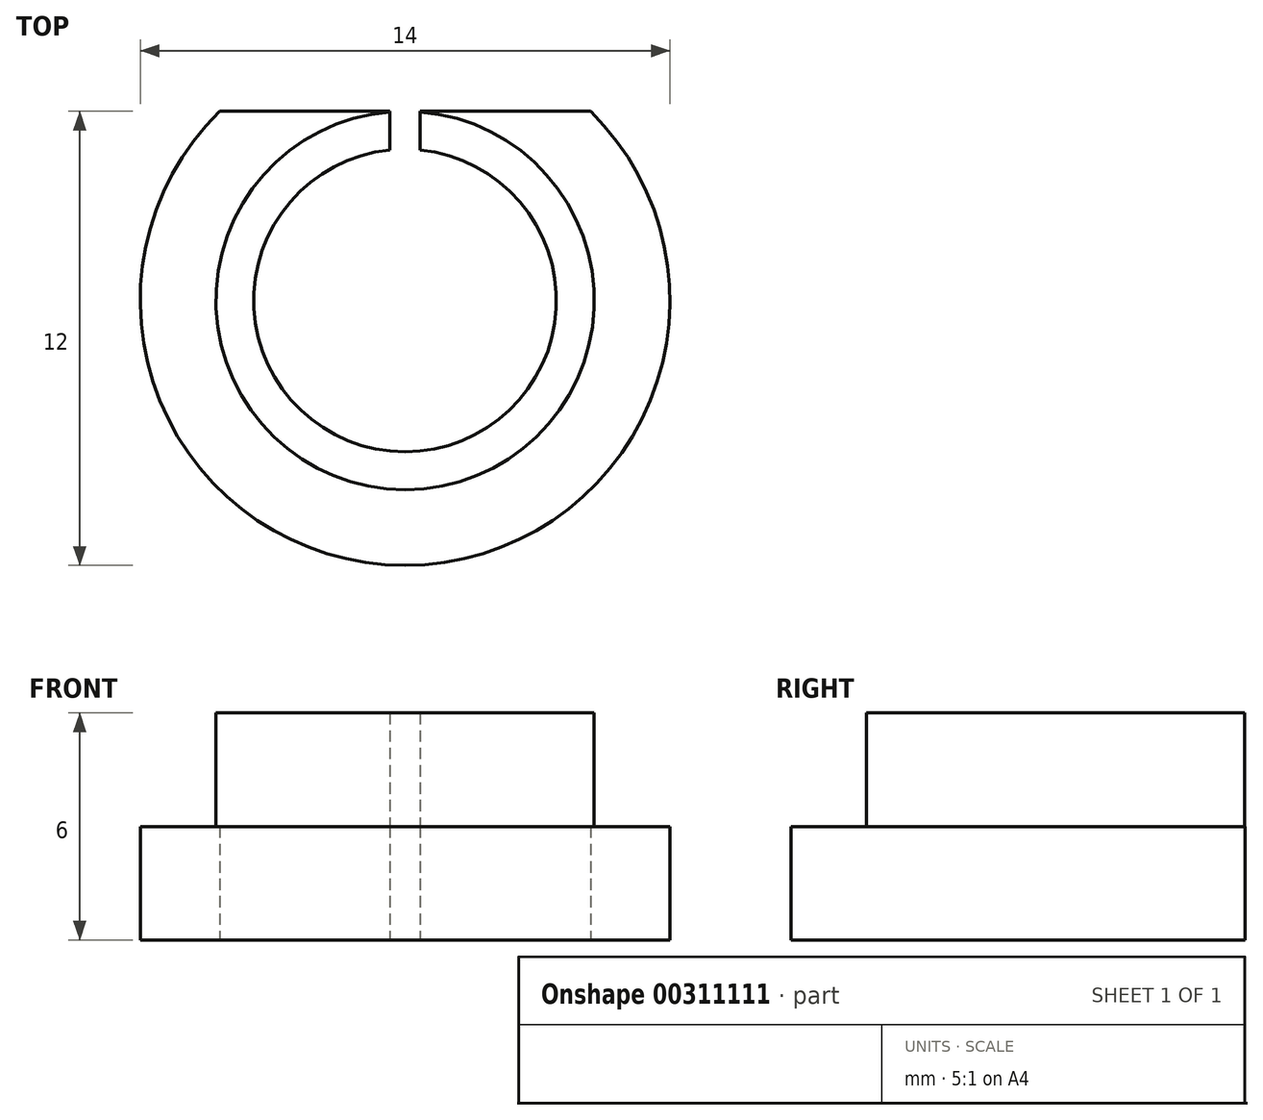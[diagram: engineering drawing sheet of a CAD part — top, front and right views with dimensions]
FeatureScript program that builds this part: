
annotation { "Feature Type Name" : "Feature", "Feature Type Description" : "" }
export const myFeature = defineFeature(function(context is Context, id is Id, definition is map)
    precondition{}
    {
        {
            var Q0;
            Q0=qCreatedBy(makeId("Top.planeOp"),FACE);
            var sketch = newSketch(context, id + "F0", { "sketchPlane" : qUnion([Q0])});
            skCircle(sketch, "E0", {"center": v(0, 0) * mm, "radius": 4 * mm});
            skCircle(sketch, "E1", {"center": v(0, 0) * mm, "radius": 7 * mm});
            skSolve(sketch);
        }
        {
            var Q0;
            Q0 = qSketchRegion(id + "F0", true);
            extrude(context, id + "F1", {"entities" : qUnion([Q0]), "depth" : 3 * mm});
        }
        {
            var Q0;
            Q0=makeQuery(id+"F1.opExtrude","CAP_FACE",FACE,{"disambiguationData":[OSD([sQuery(id+"F0.wireOp",EDGE,"E0"),sQuery(id+"F0.wireOp",EDGE,"E1")])],"isStart":false});
            var sketch = newSketch(context, id + "F2", { "sketchPlane" : qUnion([Q0])});
            skCircle(sketch, "E2", {"center": v(0, 0) * mm, "radius": 4 * mm});
            skCircle(sketch, "E3", {"center": v(0, 0) * mm, "radius": 5 * mm});
            skSolve(sketch);
        }
        {
            var Q0;
            Q0 = qSketchRegion(id + "F2", true);
            extrude(context, id + "F3", {"entities" : qUnion([Q0]), "operationType" : NewBodyOperationType.ADD, "depth" : 3 * mm});
        }
        {
            var Q0;
            Q0=qCreatedBy(makeId("Top.planeOp"),FACE);
            var sketch = newSketch(context, id + "F4", { "sketchPlane" : qUnion([Q0])});
            skArc(sketch, "E4.0", {"start": v(4.9, 5) * mm, "mid": v(0, 7) * mm, "end": v(-4.9, 5) * mm});
            skLineSegment(sketch, "E5", {"start": v(0, 5) * mm, "end": v(4.9, 5) * mm});
            skLineSegment(sketch, "E6", {"start": v(0, 5) * mm, "end": v(-4.9, 5) * mm});
            skLineSegment(sketch, "E7", {"start": v(-0.4, 5) * mm, "end": v(-0.4, 3.38) * mm});
            skLineSegment(sketch, "E8", {"start": v(-0.4, 3.38) * mm, "end": v(0.4, 3.38) * mm});
            skLineSegment(sketch, "E9", {"start": v(0.4, 3.38) * mm, "end": v(0.4, 5) * mm});
            skSolve(sketch);
        }
        {
            var Q0;
            Q0 = qSketchRegion(id + "F4", true);
            var Q1;
            Q1=makeQuery(id+"F3.opExtrude","CAP_FACE",FACE,{"disambiguationData":[OSD([sQuery(id+"F2.wireOp",EDGE,"E2"),sQuery(id+"F2.wireOp",EDGE,"E3")])],"isStart":false});
            extrude(context, id + "F5", {"entities" : qUnion([Q0]), "operationType" : NewBodyOperationType.REMOVE, "endBound" : BoundingType.UP_TO_SURFACE, "endBoundEntityFace" : qUnion([Q1]), "depth" : 25 * mm});
        }
    });
